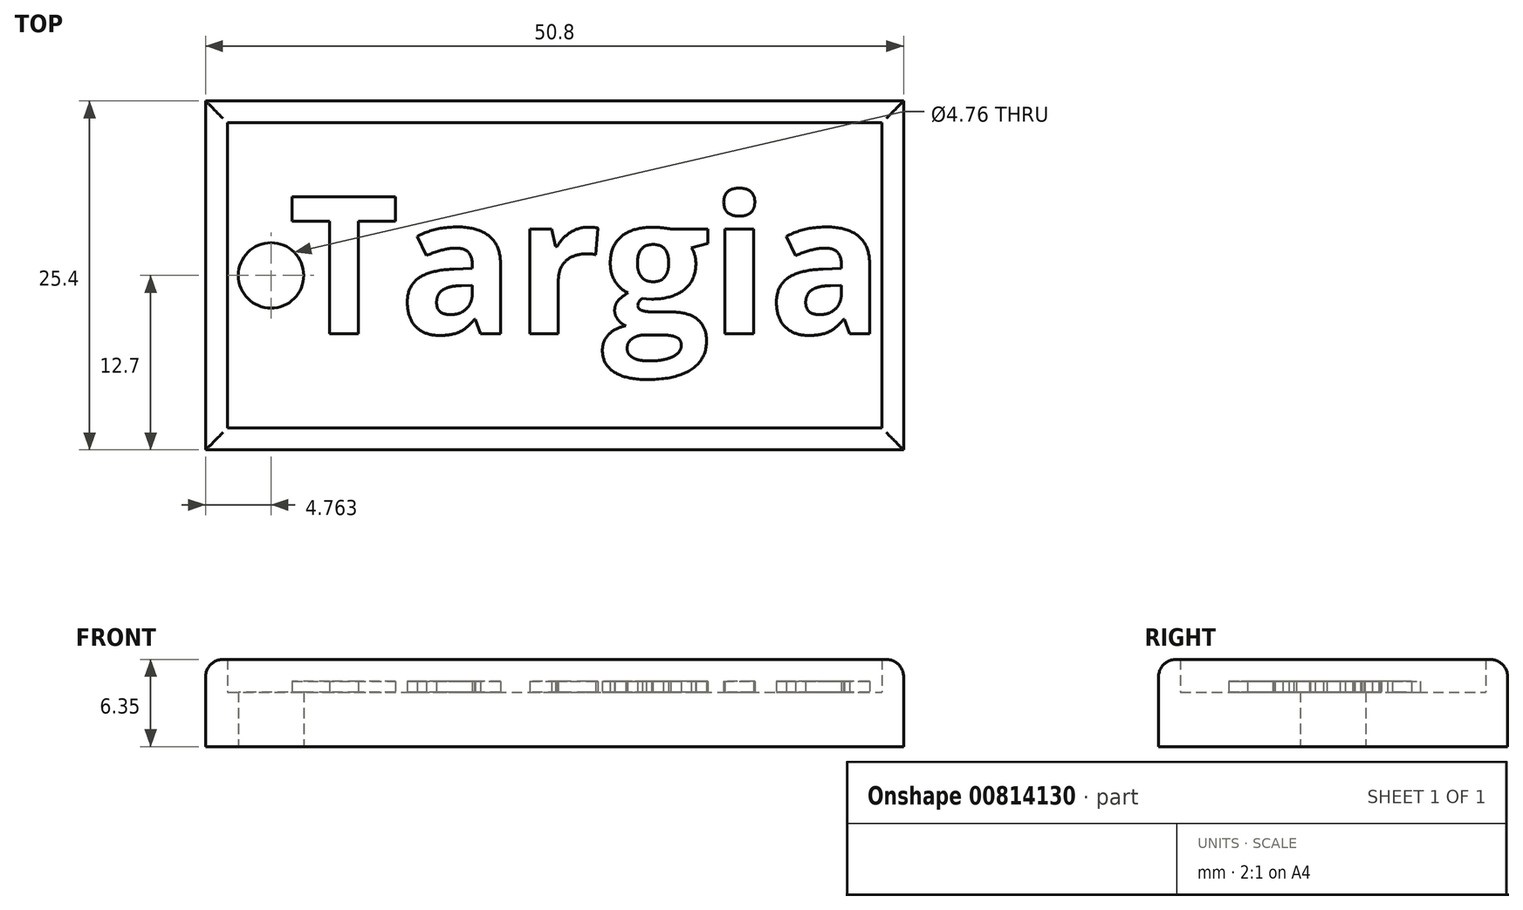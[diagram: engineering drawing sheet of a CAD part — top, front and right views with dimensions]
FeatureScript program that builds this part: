
annotation { "Feature Type Name" : "Feature", "Feature Type Description" : "" }
export const myFeature = defineFeature(function(context is Context, id is Id, definition is map)
    precondition{}
    {
        {
            var Q0;
            Q0=qCreatedBy(makeId("Top.planeOp"),FACE);
            var sketch = newSketch(context, id + "F0", { "sketchPlane" : qUnion([Q0])});
            skLineSegment(sketch, "E0.bottom", {"start": v(0, 0) * mm, "end": v(50.8, 0) * mm});
            skLineSegment(sketch, "E0.top", {"start": v(0, 25.4) * mm, "end": v(50.8, 25.4) * mm});
            skLineSegment(sketch, "E0.left", {"start": v(0, 0) * mm, "end": v(0, 25.4) * mm});
            skLineSegment(sketch, "E0.right", {"start": v(50.8, 0) * mm, "end": v(50.8, 25.4) * mm});
            skCircle(sketch, "E1", {"center": v(4.76, 12.7) * mm, "radius": 2.38 * mm});
            skPoint(sketch, "E1.centerSnap0", {"position": v(0, 12.7) * mm});
            skLineSegment(sketch, "E2.0", {"start": v(1.59, 23.81) * mm, "end": v(49.21, 23.81) * mm});
            skLineSegment(sketch, "E2.1", {"start": v(1.59, 1.59) * mm, "end": v(1.59, 23.81) * mm});
            skLineSegment(sketch, "E2.2", {"start": v(1.59, 1.59) * mm, "end": v(49.21, 1.59) * mm});
            skLineSegment(sketch, "E2.3", {"start": v(49.21, 1.59) * mm, "end": v(49.21, 23.81) * mm});
            skSolve(sketch);
        }
        {
            var Q0;
            Q0=makeQuery(id+"F0.imprint","IMPRINT",FACE,{"disambiguationData":[TD([[makeQuery(id+"F0.imprint","IMPRINT",EDGE,{"derivedFrom":sQuery(id+"F0.wireOp",EDGE,"E1")}),-1.0]])]});
            extrude(context, id + "F1", {"entities" : qUnion([Q0]), "depth" : 4.76 * mm, "offsetDistance" : 25.4 * mm});
        }
        {
            var Q0;
            Q0 = qSketchRegion(id + "F0", true);
            extrude(context, id + "F2", {"entities" : qUnion([Q0]), "operationType" : NewBodyOperationType.ADD, "depth" : 6.35 * mm, "offsetDistance" : 25.4 * mm});
        }
        {
            var Q0;
            Q0=makeQuery(id+"F2.opExtrude","CAP_EDGE",EDGE,{"disambiguationData":[OSD([sQuery(id+"F0.wireOp",EDGE,"E0.bottom")])],"isStart":false});
            var Q1;
            Q1=makeQuery(id+"F2.opExtrude","CAP_EDGE",EDGE,{"disambiguationData":[OSD([sQuery(id+"F0.wireOp",EDGE,"E0.right")])],"isStart":false});
            var Q2;
            Q2=makeQuery(id+"F2.opExtrude","CAP_EDGE",EDGE,{"disambiguationData":[OSD([sQuery(id+"F0.wireOp",EDGE,"E0.top")])],"isStart":false});
            var Q3;
            Q3=makeQuery(id+"F2.opExtrude","CAP_EDGE",EDGE,{"disambiguationData":[OSD([sQuery(id+"F0.wireOp",EDGE,"E0.left")])],"isStart":false});
            fillet(context, id + "F3", {"entities" : qUnion([Q0, Q1, Q2, Q3]), "radius" : 1.27 * mm, "tangentPropagation" : true, "allowEdgeOverflow" : false});
        }
        {
            var Q0;
            Q0=makeQuery(id+"F1.opExtrude","CAP_FACE",FACE,{"disambiguationData":[OSD([sQuery(id+"F0.wireOp",EDGE,"E1"),sQuery(id+"F0.wireOp",EDGE,"E2.0"),sQuery(id+"F0.wireOp",EDGE,"E2.1"),sQuery(id+"F0.wireOp",EDGE,"E2.2"),sQuery(id+"F0.wireOp",EDGE,"E2.3")])],"isStart":false});
            extrude(context, id + "F4", {"entities" : qUnion([Q0]), "operationType" : NewBodyOperationType.REMOVE, "oppositeDirection" : true, "depth" : 1.59 * mm, "offsetDistance" : 25.4 * mm});
        }
        {
            var Q0;
            Q0=makeQuery(id+"F4.boolean.opBoolean","COPY",FACE,{"derivedFrom":makeQuery(id+"F4.opExtrude","CAP_FACE",FACE,{"disambiguationData":[OSD([sQuery(id+"F0.wireOp",EDGE,"E1"),sQuery(id+"F0.wireOp",EDGE,"E2.0"),sQuery(id+"F0.wireOp",EDGE,"E2.1"),sQuery(id+"F0.wireOp",EDGE,"E2.2"),sQuery(id+"F0.wireOp",EDGE,"E2.3")])],"isStart":false})});
            extrude(context, id + "F5", {"entities" : qUnion([Q0]), "operationType" : NewBodyOperationType.ADD, "depth" : 0.8 * mm, "offsetDistance" : 25.4 * mm});
        }
        {
            var Q0;
            Q0=makeQuery(id+"F5.opExtrude","CAP_FACE",FACE,{"disambiguationData":[OSD([sQuery(id+"F0.wireOp",EDGE,"E1"),sQuery(id+"F0.wireOp",EDGE,"E2.0"),sQuery(id+"F0.wireOp",EDGE,"E2.1"),sQuery(id+"F0.wireOp",EDGE,"E2.2"),sQuery(id+"F0.wireOp",EDGE,"E2.3")])],"isStart":false});
            var sketch = newSketch(context, id + "F6", { "sketchPlane" : qUnion([Q0])});
            skText(sketch, "E3", { "text": "Targia", "fontName": "OpenSans-Bold.ttf"});
            const initialGuessF6  = {"E3": [0.00603, 0.00847, 1, 0, 0.01003]};
            skSetInitialGuess(sketch, initialGuessF6);
            skSolve(sketch);
        }
        {
            var Q0;
            Q0 = qSketchRegion(id + "F6", true);
            extrude(context, id + "F7", {"entities" : qUnion([Q0]), "operationType" : NewBodyOperationType.ADD, "depth" : 0.8 * mm, "offsetDistance" : 25.4 * mm});
        }
    });
